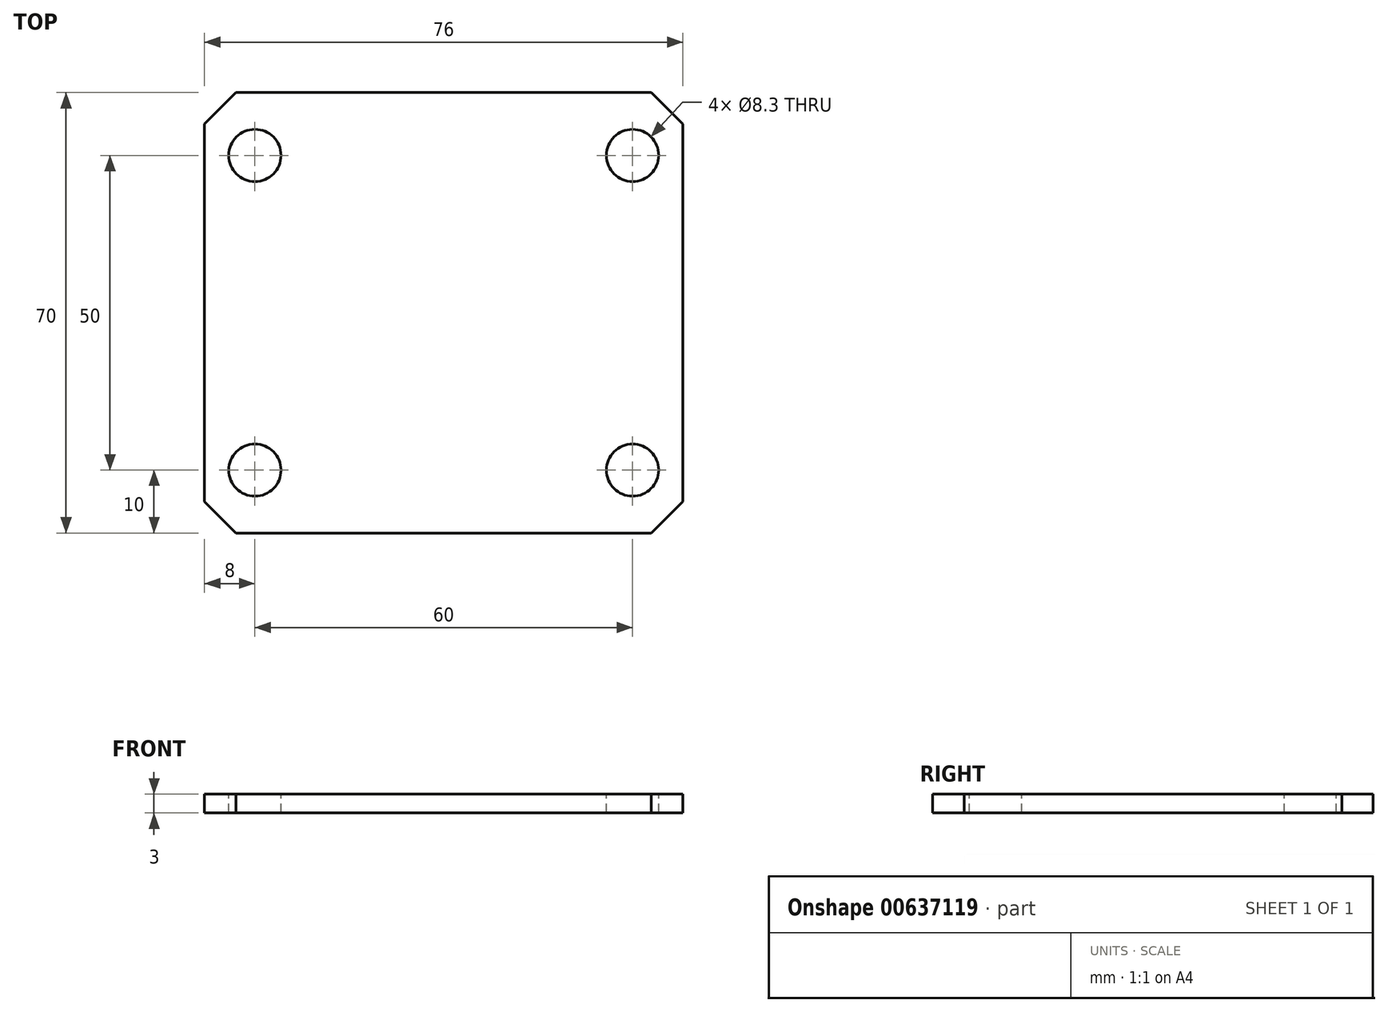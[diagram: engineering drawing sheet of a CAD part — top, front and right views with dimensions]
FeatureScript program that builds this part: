
annotation { "Feature Type Name" : "Feature", "Feature Type Description" : "" }
export const myFeature = defineFeature(function(context is Context, id is Id, definition is map)
    precondition{}
    {
        {
            var Q0;
            Q0=qCreatedBy(makeId("Top.planeOp"),FACE);
            var sketch = newSketch(context, id + "F0", { "sketchPlane" : qUnion([Q0])});
            skLineSegment(sketch, "E0.bottom", {"start": v(-38, 35) * mm, "end": v(38, 35) * mm});
            skLineSegment(sketch, "E0.top", {"start": v(-38, -35) * mm, "end": v(38, -35) * mm});
            skLineSegment(sketch, "E0.left", {"start": v(-38, 35) * mm, "end": v(-38, -35) * mm});
            skLineSegment(sketch, "E0.right", {"start": v(38, 35) * mm, "end": v(38, -35) * mm});
            skLineSegment(sketch, "E1", {"start": v(-38, 0) * mm, "end": v(0, 35) * mm, "construction": true});
            skSolve(sketch);
        }
        {
            var Q0;
            Q0 = qSketchRegion(id + "F0", true);
            extrude(context, id + "F1", {"entities" : qUnion([Q0]), "oppositeDirection" : true, "depth" : 3 * mm, "offsetDistance" : 25 * mm});
        }
        {
            var Q0;
            Q0=makeQuery(id+"F1.opExtrude","CAP_FACE",FACE,{"disambiguationData":[OSD([sQuery(id+"F0.wireOp",EDGE,"E0.bottom"),sQuery(id+"F0.wireOp",EDGE,"E0.top"),sQuery(id+"F0.wireOp",EDGE,"E0.left"),sQuery(id+"F0.wireOp",EDGE,"E0.right")])],"isStart":true});
            var sketch = newSketch(context, id + "F2", { "sketchPlane" : qUnion([Q0])});
            skLineSegment(sketch, "E2.bottom", {"start": v(-30, 25) * mm, "end": v(30, 25) * mm, "construction": true});
            skLineSegment(sketch, "E2.top", {"start": v(-30, -25) * mm, "end": v(30, -25) * mm, "construction": true});
            skLineSegment(sketch, "E2.left", {"start": v(-30, 25) * mm, "end": v(-30, -25) * mm, "construction": true});
            skLineSegment(sketch, "E2.right", {"start": v(30, 25) * mm, "end": v(30, -25) * mm, "construction": true});
            skPoint(sketch, "E3.startSnap0", {"position": v(-38, 0) * mm});
            skLineSegment(sketch, "E4", {"start": v(-30, 0) * mm, "end": v(0, 25) * mm, "construction": true});
            skSolve(sketch);
        }
        {
            var Q0;
            Q0=sQuery(id+"F2.wireOp",VERTEX,"E2.left.start");
            var Q1;
            Q1=sQuery(id+"F2.wireOp",VERTEX,"E2.right.start");
            var Q2;
            Q2=sQuery(id+"F2.wireOp",VERTEX,"E2.top.end");
            var Q3;
            Q3=sQuery(id+"F2.wireOp",VERTEX,"E2.left.end");
            var Q4;
            Q4=makeQuery(id+"F1.opExtrude","SWEPT_BODY",BODY,{"disambiguationData":[OSD([sQuery(id+"F0.wireOp",EDGE,"E0.bottom"),sQuery(id+"F0.wireOp",EDGE,"E0.top"),sQuery(id+"F0.wireOp",EDGE,"E0.left"),sQuery(id+"F0.wireOp",EDGE,"E0.right")])]});
            hole(context, id + "F3", {"style" : HoleStyle.SIMPLE, "endStyle" : HoleEndStyle.THROUGH, "holeDiameter" : 8.3 * mm, "majorDiameter" : 5 * mm, "isTappedThrough" : true, "tappedDepth" : 12 * mm, "tapClearance" : 3, "startFromSketch" : true, "locations" : qUnion([Q0, Q1, Q2, Q3]), "scope" : qUnion([Q4])});
        }
        {
            var Q0;
            Q0=makeQuery(id+"F1.opExtrude","SWEPT_EDGE",EDGE,{"disambiguationData":[OSD([sQuery(id+"F0.wireOp",EDGE,"E0.bottom"),sQuery(id+"F0.wireOp",EDGE,"E0.left")])]});
            var Q1;
            Q1=makeQuery(id+"F1.opExtrude","SWEPT_EDGE",EDGE,{"disambiguationData":[OSD([sQuery(id+"F0.wireOp",EDGE,"E0.top"),sQuery(id+"F0.wireOp",EDGE,"E0.left")])]});
            var Q2;
            Q2=makeQuery(id+"F1.opExtrude","SWEPT_EDGE",EDGE,{"disambiguationData":[OSD([sQuery(id+"F0.wireOp",EDGE,"E0.top"),sQuery(id+"F0.wireOp",EDGE,"E0.right")])]});
            var Q3;
            Q3=makeQuery(id+"F1.opExtrude","SWEPT_EDGE",EDGE,{"disambiguationData":[OSD([sQuery(id+"F0.wireOp",EDGE,"E0.bottom"),sQuery(id+"F0.wireOp",EDGE,"E0.right")])]});
            chamfer(context, id + "F4", {"entities" : qUnion([Q0, Q1, Q2, Q3]), "width" : 5 * mm, "tangentPropagation" : true});
        }
    });
